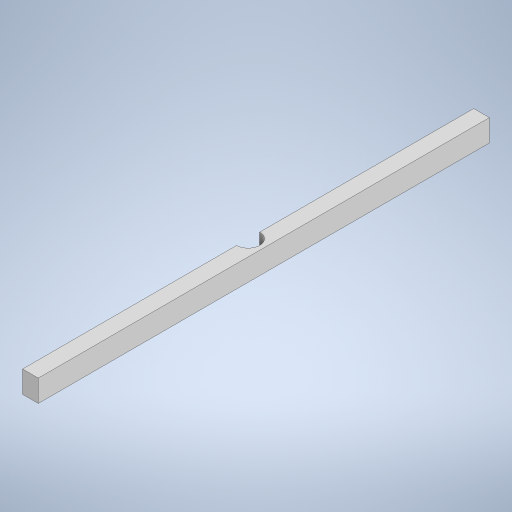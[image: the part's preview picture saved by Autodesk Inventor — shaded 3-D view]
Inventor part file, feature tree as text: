
AUTODESK INVENTOR PART (.ipt)
format: ipt  version: 2023 (Build 270158000, 158)  size: 242,688 bytes
history: native  units: in
note: dims shown in document units (in); Inventor stores cm internally (conversion verified against a paired STEP export)
features: extrude x1, sketch x1
ambient origin geometry x8: Origin, YZ Plane, XZ Plane, XY Plane, X Axis, Y Axis, Z Axis, Center Point
bodies: Solid1 (feature_tree)
feature tree (2):
  extrude  "Extrusion1"  Depth=0.0591in
  sketch  "Sketch1"  dims[d0=1.6969in d1=0.0591in d2=0.0433in d3=0.0827in d4=0.0in]
